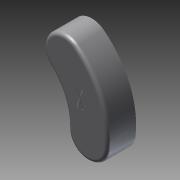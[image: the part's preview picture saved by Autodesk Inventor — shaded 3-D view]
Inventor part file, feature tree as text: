
AUTODESK INVENTOR PART (.ipt)
format: ipt  version: 2012 SP1 (Build 160190100, 190)  size: 123,392 bytes
history: native  units: in
note: dims shown in document units (in); Inventor stores cm internally (conversion verified against a paired STEP export)
features: extrude x2, sketch x2, fillet x1
ambient origin geometry x8: Origin, YZ Plane, XZ Plane, XY Plane, X Axis, Y Axis, Z Axis, Center Point
bodies: Solid1 (feature_tree)
feature tree (5):
  extrude  "Extrusion1"  Depth=0.2in TaperAngle=0.0deg
  fillet  "Fillet1"  Radius=0.025in
  extrude  "Extrusion2"  [1 undecoded]
  sketch  "Sketch1"  dims[d3=0.278in d4=0.278in d5=0.2in d6=0.0in d7=0.025in]
  sketch  "Sketch2"  dims[d8=0.0025in d9=0.0in]
note: 1 required parameter value undecoded (feature->parameter linkage not recoverable at this tier; creation-order binding heuristic only, values carry confidence <= 0.55)
